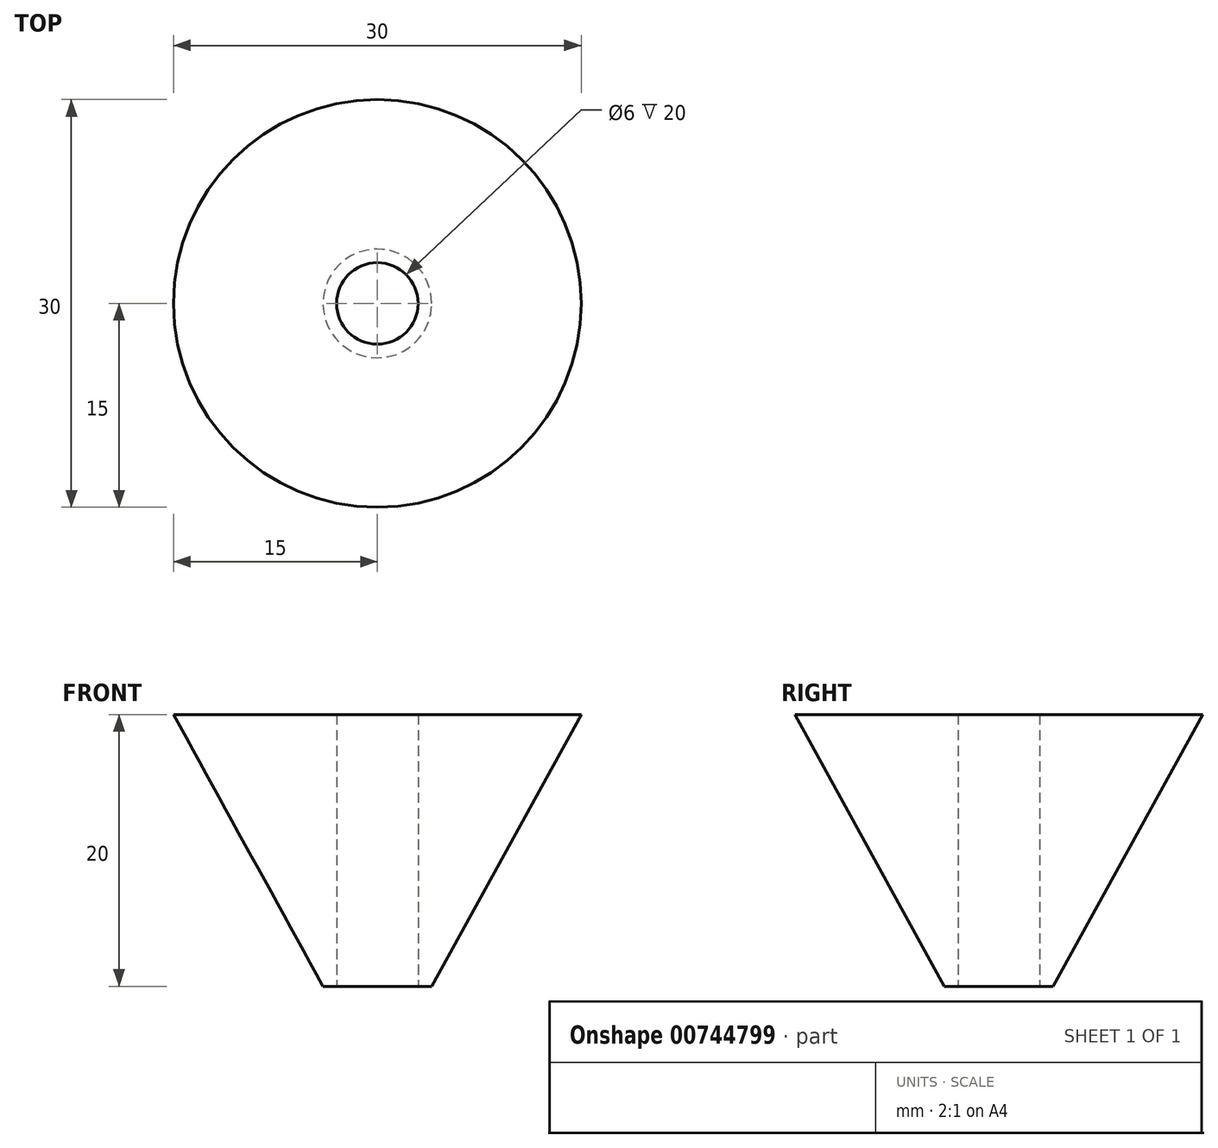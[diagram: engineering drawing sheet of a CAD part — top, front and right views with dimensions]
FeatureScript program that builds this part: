
annotation { "Feature Type Name" : "Feature", "Feature Type Description" : "" }
export const myFeature = defineFeature(function(context is Context, id is Id, definition is map)
    precondition{}
    {
        {
            var Q0;
            Q0=qCreatedBy(makeId("Front.planeOp"),FACE);
            var sketch = newSketch(context, id + "F0", { "sketchPlane" : qUnion([Q0])});
            skLineSegment(sketch, "E0", {"start": v(-15, 37.92) * mm, "end": v(-4, 17.92) * mm});
            skLineSegment(sketch, "E1", {"start": v(-4, 17.92) * mm, "end": v(-3, 17.92) * mm});
            skLineSegment(sketch, "E2", {"start": v(-3, 17.92) * mm, "end": v(-3, 37.45) * mm});
            skLineSegment(sketch, "E3", {"start": v(-15, 37.92) * mm, "end": v(-3, 37.92) * mm});
            skLineSegment(sketch, "E4", {"start": v(-3, 37.45) * mm, "end": v(-3, 37.92) * mm});
            skLineSegment(sketch, "E5", {"start": v(0, 14.54) * mm, "end": v(0, 52.5) * mm, "construction": true});
            skSolve(sketch);
        }
        {
            var Q0;
            Q0=makeQuery(id+"F0.imprint","IMPRINT",FACE,{"disambiguationData":[TD([[makeQuery(id+"F0.imprint","IMPRINT",EDGE,{"derivedFrom":sQuery(id+"F0.wireOp",EDGE,"E0")}),1.0]])]});
            var Q1;
            Q1=sQuery(id+"F0.wireOp",EDGE,"E5");
            var Q2;
            Q2=sQuery(id+"F0.wireOp",EDGE,"E5");
            revolve(context, id + "F1", {"surfaceOperationType" : NewSurfaceOperationType.NEW, "entities" : qUnion([Q0]), "surfaceEntities" : qUnion([Q1]), "axis" : qUnion([Q2]), "revolveType" : RevolveType.FULL});
        }
    });
